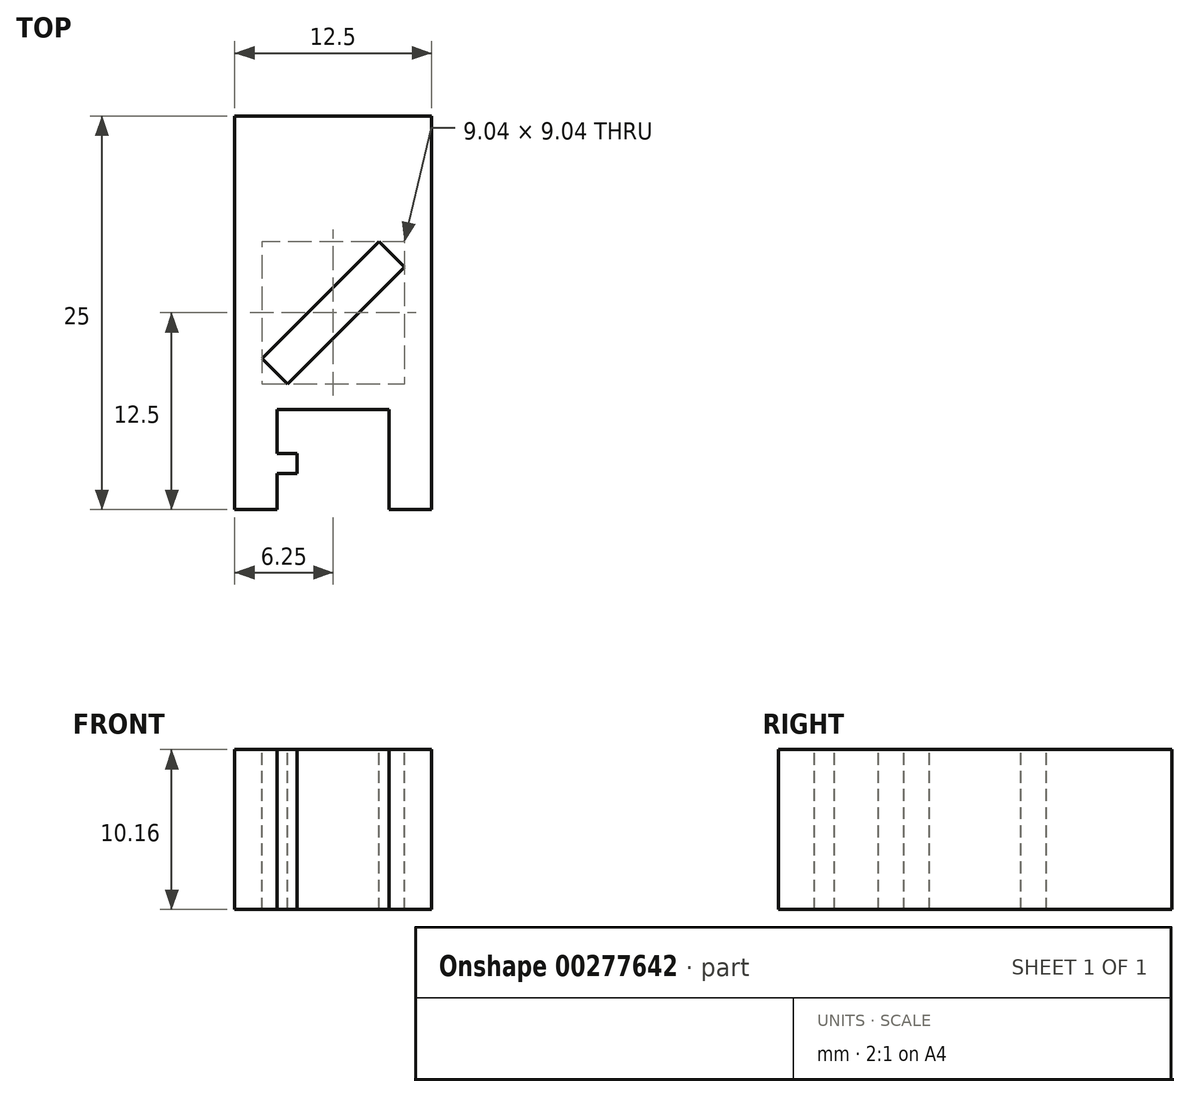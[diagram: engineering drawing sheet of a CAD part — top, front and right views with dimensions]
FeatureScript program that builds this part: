
annotation { "Feature Type Name" : "Feature", "Feature Type Description" : "" }
export const myFeature = defineFeature(function(context is Context, id is Id, definition is map)
    precondition{}
    {
        {
            var Q0;
            Q0=qCreatedBy(makeId("Top.planeOp"),FACE);
            var sketch = newSketch(context, id + "F0", { "sketchPlane" : qUnion([Q0])});
            skLineSegment(sketch, "E0.bottom", {"start": v(6.25, -12.5) * mm, "end": v(-6.25, -12.5) * mm});
            skLineSegment(sketch, "E0.top", {"start": v(6.25, 12.5) * mm, "end": v(-6.25, 12.5) * mm});
            skLineSegment(sketch, "E0.left", {"start": v(6.25, -12.5) * mm, "end": v(6.25, 12.5) * mm});
            skLineSegment(sketch, "E0.right", {"start": v(-6.25, -12.5) * mm, "end": v(-6.25, 12.5) * mm});
            skPoint(sketch, "E0.middle", {"position": v(0, 0) * mm});
            skSolve(sketch);
        }
        {
            var Q0;
            Q0=makeQuery(id+"F0.imprint","IMPRINT",FACE,{"disambiguationData":[TD([[makeQuery(id+"F0.imprint","IMPRINT",EDGE,{"derivedFrom":sQuery(id+"F0.wireOp",EDGE,"E0.bottom")}),-1.0]])]});
            extrude(context, id + "F1", {"entities" : qUnion([Q0]), "depth" : 10.16 * mm});
        }
        {
            var Q0;
            Q0=makeQuery(id+"F1.opExtrude","CAP_FACE",FACE,{"disambiguationData":[OSD([sQuery(id+"F0.wireOp",EDGE,"E0.bottom"),sQuery(id+"F0.wireOp",EDGE,"E0.top"),sQuery(id+"F0.wireOp",EDGE,"E0.left"),sQuery(id+"F0.wireOp",EDGE,"E0.right")])],"isStart":false});
            var sketch = newSketch(context, id + "F2", { "sketchPlane" : qUnion([Q0])});
            skLineSegment(sketch, "E1.bottom", {"start": v(-3.56, -12.5) * mm, "end": v(3.56, -12.5) * mm});
            skLineSegment(sketch, "E1.top", {"start": v(-3.56, -6.15) * mm, "end": v(3.56, -6.15) * mm});
            skLineSegment(sketch, "E1.left", {"start": v(-3.56, -12.5) * mm, "end": v(-3.56, -6.15) * mm});
            skLineSegment(sketch, "E1.right", {"start": v(3.56, -12.5) * mm, "end": v(3.56, -6.15) * mm});
            skSolve(sketch);
        }
        {
            var Q0;
            Q0=makeQuery(id+"F2.imprint","IMPRINT",FACE,{"disambiguationData":[TD([[makeQuery(id+"F2.imprint","IMPRINT",EDGE,{"derivedFrom":sQuery(id+"F2.wireOp",EDGE,"E1.bottom")}),-1.0]])]});
            extrude(context, id + "F3", {"entities" : qUnion([Q0]), "operationType" : NewBodyOperationType.REMOVE, "oppositeDirection" : true, "depth" : 25.4 * mm});
        }
        {
            var Q0;
            Q0=makeQuery(id+"F1.opExtrude","CAP_FACE",FACE,{"disambiguationData":[OSD([sQuery(id+"F0.wireOp",EDGE,"E0.bottom"),sQuery(id+"F0.wireOp",EDGE,"E0.top"),sQuery(id+"F0.wireOp",EDGE,"E0.left"),sQuery(id+"F0.wireOp",EDGE,"E0.right")])],"isStart":false});
            var sketch = newSketch(context, id + "F4", { "sketchPlane" : qUnion([Q0])});
            skLineSegment(sketch, "E2.bottom", {"start": v(-3.56, -8.94) * mm, "end": v(-2.29, -8.94) * mm});
            skLineSegment(sketch, "E2.top", {"start": v(-3.56, -10.21) * mm, "end": v(-2.29, -10.21) * mm});
            skLineSegment(sketch, "E2.left", {"start": v(-3.56, -8.94) * mm, "end": v(-3.56, -10.21) * mm});
            skLineSegment(sketch, "E2.right", {"start": v(-2.29, -8.94) * mm, "end": v(-2.29, -10.21) * mm});
            skSolve(sketch);
        }
        {
            var Q0;
            Q0=makeQuery(id+"F4.imprint","IMPRINT",FACE,{"disambiguationData":[TD([[makeQuery(id+"F4.imprint","IMPRINT",EDGE,{"derivedFrom":sQuery(id+"F4.wireOp",EDGE,"E2.bottom")}),-1.0]])]});
            var Q1;
            Q1=makeQuery(id+"F1.opExtrude","CAP_FACE",FACE,{"disambiguationData":[OSD([sQuery(id+"F0.wireOp",EDGE,"E0.bottom"),sQuery(id+"F0.wireOp",EDGE,"E0.top"),sQuery(id+"F0.wireOp",EDGE,"E0.left"),sQuery(id+"F0.wireOp",EDGE,"E0.right")])],"isStart":true});
            extrude(context, id + "F5", {"entities" : qUnion([Q0]), "operationType" : NewBodyOperationType.ADD, "endBound" : BoundingType.UP_TO_SURFACE, "oppositeDirection" : true, "endBoundEntityFace" : qUnion([Q1]), "depth" : 25.4 * mm});
        }
        {
            var Q0;
            Q0=qCreatedBy(makeId("Front.planeOp"),FACE);
            var sketch = newSketch(context, id + "F6", { "sketchPlane" : qUnion([Q0])});
            skLineSegment(sketch, "E3", {"start": v(0, 0) * mm, "end": v(0, 39.35) * mm});
            skSolve(sketch);
        }
        {
            var Q0;
            {var subQ0=sQuery(id+"F4.wireOp",EDGE,"E2.right");var subQ1=sQuery(id+"F4.wireOp",EDGE,"E2.left");var subQ2=sQuery(id+"F4.wireOp",EDGE,"E2.top");var subQ3=sQuery(id+"F4.wireOp",EDGE,"E2.bottom");Q0=makeQuery(id+"FZ99muYWaTXzHZh_1.1.F9qQpSXjTnUJ7Ic_1.1.F5.boolean.opBoolean","MERGE",FACE,{"derivedFrom":[makeQuery(id+"FZ99muYWaTXzHZh_1.1.F5.boolean.opBoolean","MERGE",FACE,{"derivedFrom":[makeQuery(id+"F9qQpSXjTnUJ7Ic_1.1.F5.boolean.opBoolean","MERGE",FACE,{"derivedFrom":[makeQuery(id+"F5.boolean.opBoolean","MERGE",FACE,{"derivedFrom":[makeQuery(id+"F1.opExtrude","CAP_FACE",FACE,{"disambiguationData":[OSD([sQuery(id+"F0.wireOp",EDGE,"E0.bottom"),sQuery(id+"F0.wireOp",EDGE,"E0.top"),sQuery(id+"F0.wireOp",EDGE,"E0.left"),sQuery(id+"F0.wireOp",EDGE,"E0.right")])],"isStart":false}),makeQuery(id+"F5.opExtrude","CAP_FACE",FACE,{"disambiguationData":[OSD([subQ3,subQ2,subQ1,subQ0])],"isStart":true})]}),makeQuery(id+"F9qQpSXjTnUJ7Ic_1.1.F5.opExtrude","CAP_FACE",FACE,{"disambiguationData":[OSD([subQ3,subQ2,subQ1,subQ0])],"isStart":true})]}),makeQuery(id+"FZ99muYWaTXzHZh_1.1.F5.opExtrude","CAP_FACE",FACE,{"disambiguationData":[OSD([subQ3,subQ2,subQ1,subQ0])],"isStart":true})]}),makeQuery(id+"FZ99muYWaTXzHZh_1.1.F9qQpSXjTnUJ7Ic_1.1.F5.opExtrude","CAP_FACE",FACE,{"disambiguationData":[OSD([subQ3,subQ2,subQ1,subQ0])],"isStart":true})]});}
            var sketch = newSketch(context, id + "F7", { "sketchPlane" : qUnion([Q0])});
            skLineSegment(sketch, "E4", {"start": v(-4.52, -2.9) * mm, "end": v(2.9, 4.52) * mm});
            skLineSegment(sketch, "E5", {"start": v(2.9, 4.52) * mm, "end": v(4.52, 2.9) * mm});
            skLineSegment(sketch, "E6", {"start": v(4.52, 2.9) * mm, "end": v(-2.9, -4.52) * mm});
            skLineSegment(sketch, "E7", {"start": v(-2.9, -4.52) * mm, "end": v(-4.52, -2.9) * mm});
            skLineSegment(sketch, "E8", {"start": v(-3.71, -3.71) * mm, "end": v(0, 0) * mm});
            skLineSegment(sketch, "E9", {"start": v(-0.8, 0.8) * mm, "end": v(0, 0) * mm});
            skSolve(sketch);
        }
        {
            var Q0;
            Q0=qSketchRegion(id+"F7",true);
            extrude(context, id + "F8", {"entities" : qUnion([Q0]), "operationType" : NewBodyOperationType.REMOVE, "oppositeDirection" : true, "depth" : 25.4 * mm});
        }
    });
